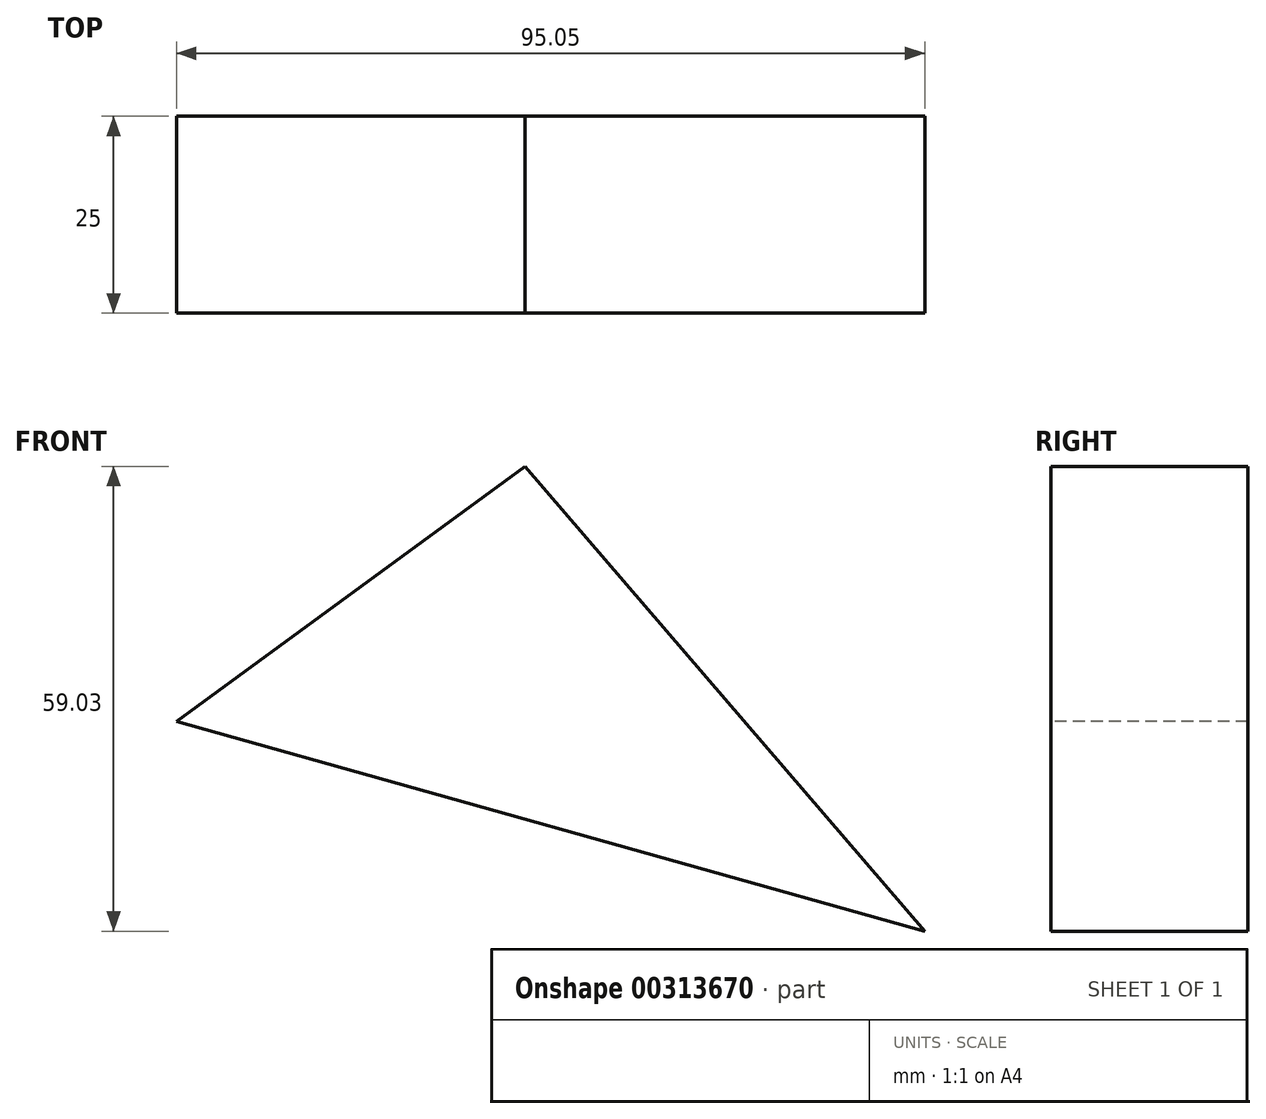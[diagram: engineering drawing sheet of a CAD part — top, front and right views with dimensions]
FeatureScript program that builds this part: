
annotation { "Feature Type Name" : "Feature", "Feature Type Description" : "" }
export const myFeature = defineFeature(function(context is Context, id is Id, definition is map)
    precondition{}
    {
        {
            var Q0;
            Q0=qCreatedBy(makeId("Front.planeOp"),FACE);
            var sketch = newSketch(context, id + "F0", { "sketchPlane" : qUnion([Q0])});
            skLineSegment(sketch, "E0", {"start": v(-58.69, 20.75) * mm, "end": v(2.8, 65.77) * mm});
            skLineSegment(sketch, "E1", {"start": v(2.8, 65.77) * mm, "end": v(53.6, 6.74) * mm});
            skLineSegment(sketch, "E2", {"start": v(53.6, 6.74) * mm, "end": v(35.4, -40.7) * mm});
            skLineSegment(sketch, "E3", {"start": v(35.4, -40.7) * mm, "end": v(-58.69, 20.75) * mm});
            skLineSegment(sketch, "E4", {"start": v(53.6, 6.74) * mm, "end": v(-41.46, 33.36) * mm});
            skSolve(sketch);
        }
        {
            var Q0;
            {var subQ0=sQuery(id+"F0.wireOp",EDGE,"E1");Q0=makeQuery(id+"F0.imprint","IMPRINT",FACE,{"disambiguationData":[TD([[makeQuery(id+"F0.imprint","IMPRINT",EDGE,{"derivedFrom":subQ0}),-1.0]])]});}
            extrude(context, id + "F1", {"entities" : qUnion([Q0]), "oppositeDirection" : true, "depth" : 25 * mm});
        }
    });
